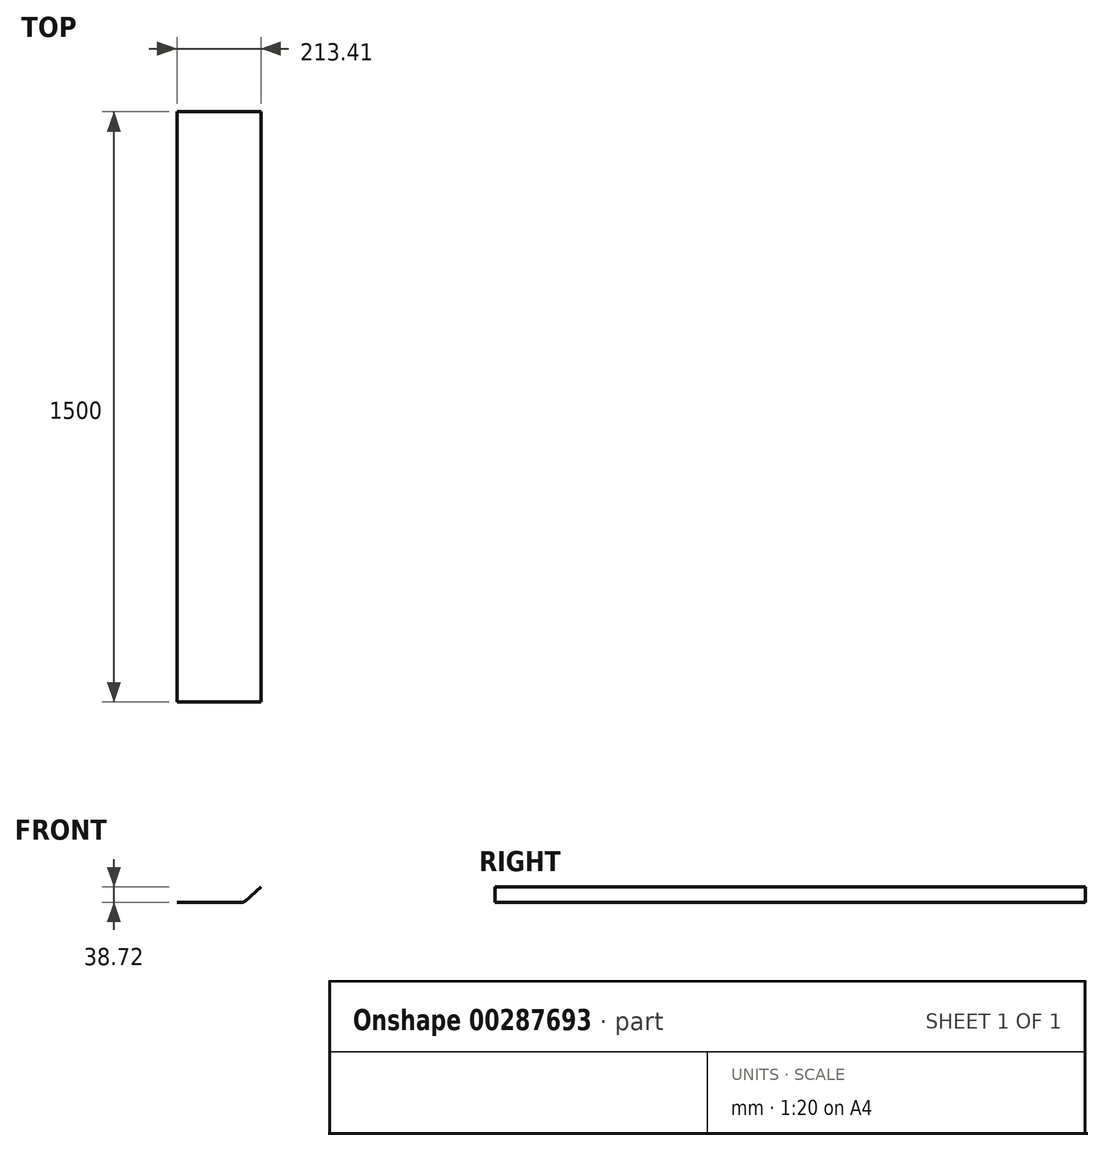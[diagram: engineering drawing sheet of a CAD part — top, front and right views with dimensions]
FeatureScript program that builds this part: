
annotation { "Feature Type Name" : "Feature", "Feature Type Description" : "" }
export const myFeature = defineFeature(function(context is Context, id is Id, definition is map)
    precondition{}
    {
        {
            var Q0;
            Q0=qCreatedBy(makeId("Front.planeOp"),FACE);
            var sketch = newSketch(context, id + "F0", { "sketchPlane" : qUnion([Q0])});
            skLineSegment(sketch, "E0", {"start": v(-36.2, 0) * mm, "end": v(-76.83, -36.18) * mm});
            skLineSegment(sketch, "E1", {"start": v(-83.48, -38.72) * mm, "end": v(-249.61, -38.72) * mm});
            skPoint(sketch, "E2.visualSharp", {"position": v(-79.68, -38.72) * mm});
            skArc(sketch, "E2.filletArc", {"start": v(-83.48, -38.72) * mm, "mid": v(-79.92, -38.06) * mm, "end": v(-76.83, -36.18) * mm});
            skSolve(sketch);
        }
        {
            var Q0;
            Q0=sQuery(id+"F0.wireOp",EDGE,"E1");
            var Q1;
            Q1=sQuery(id+"F0.wireOp",EDGE,"E2.filletArc");
            var Q2;
            Q2=sQuery(id+"F0.wireOp",EDGE,"E0");
            extrude(context, id + "F1", {"bodyType" : ToolBodyType.SURFACE, "surfaceEntities" : qUnion([Q0, Q1, Q2]), "depth" : 1500 * mm});
        }
    });
